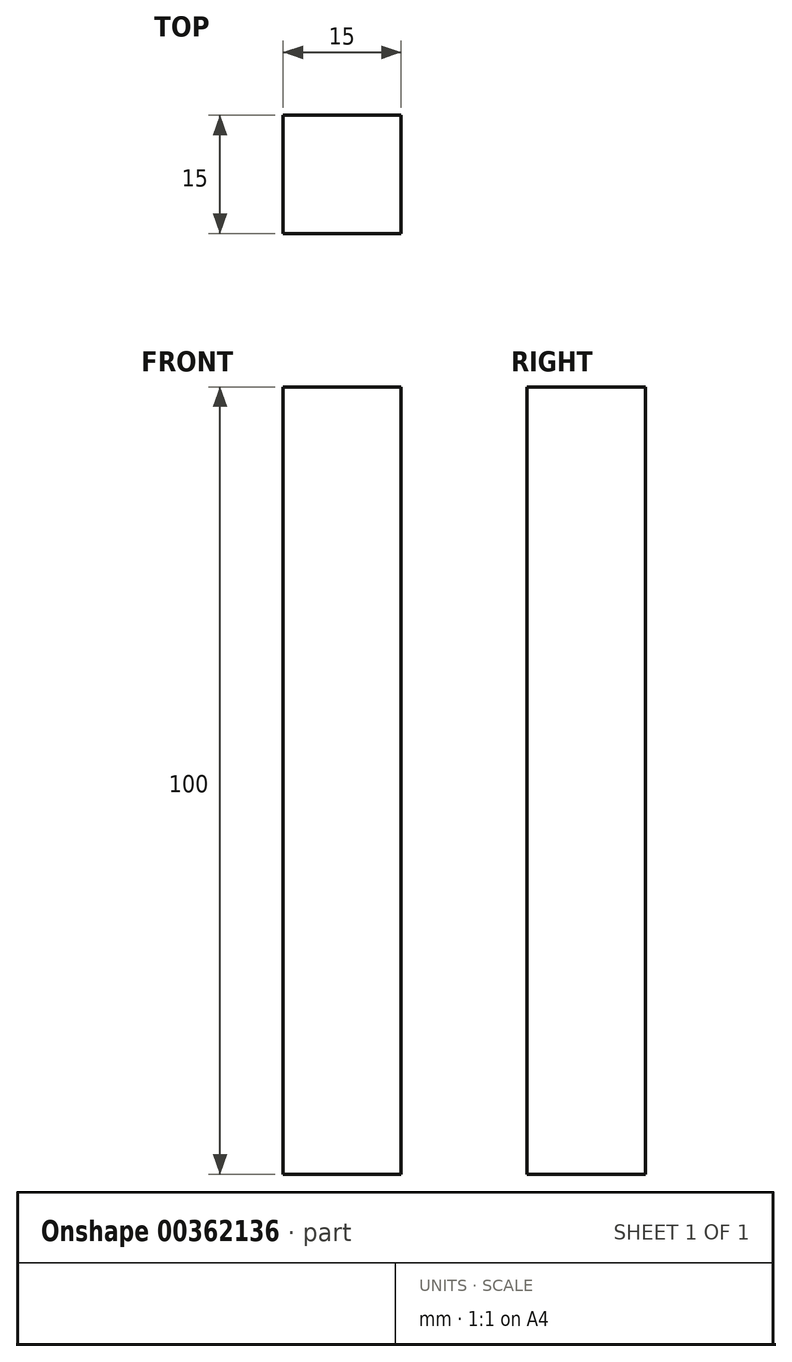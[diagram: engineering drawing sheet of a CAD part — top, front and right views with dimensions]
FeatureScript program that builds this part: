
annotation { "Feature Type Name" : "Feature", "Feature Type Description" : "" }
export const myFeature = defineFeature(function(context is Context, id is Id, definition is map)
    precondition{}
    {
        {
            var Q0;
            Q0=qCreatedBy(makeId("Top.planeOp"),FACE);
            var sketch = newSketch(context, id + "F0", { "sketchPlane" : qUnion([Q0])});
            skLineSegment(sketch, "E0.bottom", {"start": v(-7.5, 7.5) * mm, "end": v(7.5, 7.5) * mm});
            skLineSegment(sketch, "E0.top", {"start": v(-7.5, -7.5) * mm, "end": v(7.5, -7.5) * mm});
            skLineSegment(sketch, "E0.left", {"start": v(-7.5, 7.5) * mm, "end": v(-7.5, -7.5) * mm});
            skLineSegment(sketch, "E0.right", {"start": v(7.5, 7.5) * mm, "end": v(7.5, -7.5) * mm});
            skPoint(sketch, "E0.middle", {"position": v(0, 0) * mm});
            skSolve(sketch);
        }
        {
            var Q0;
            Q0=makeQuery(id+"F0.imprint","IMPRINT",FACE,{"disambiguationData":[TD([[makeQuery(id+"F0.imprint","IMPRINT",EDGE,{"derivedFrom":sQuery(id+"F0.wireOp",EDGE,"E0.bottom")}),-1.0]])]});
            extrude(context, id + "F1", {"entities" : qUnion([Q0]), "depth" : 100 * mm, "offsetDistance" : 25 * mm});
        }
    });
